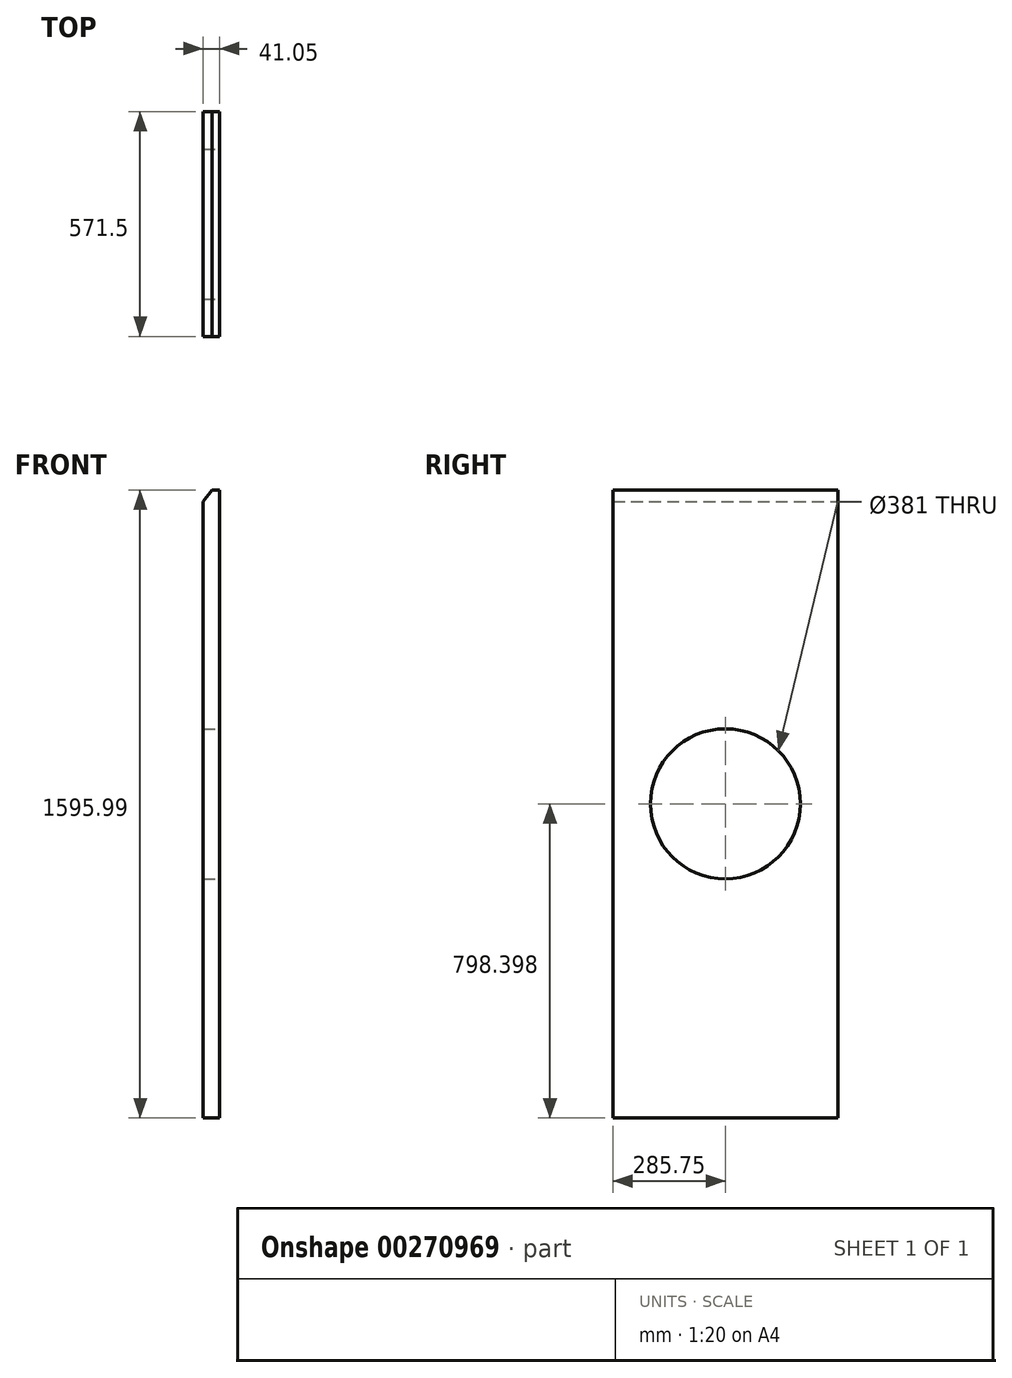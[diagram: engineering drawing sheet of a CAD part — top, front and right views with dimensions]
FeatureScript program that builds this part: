
annotation { "Feature Type Name" : "Feature", "Feature Type Description" : "" }
export const myFeature = defineFeature(function(context is Context, id is Id, definition is map)
    precondition{}
    {
        {
            var Q0;
            Q0=qCreatedBy(makeId("Front.planeOp"),FACE);
            var sketch = newSketch(context, id + "F0", { "sketchPlane" : qUnion([Q0])});
            skLineSegment(sketch, "E0", {"start": v(0, 0) * mm, "end": v(0, 1595.18) * mm});
            skLineSegment(sketch, "E1", {"start": v(0, 1595.18) * mm, "end": v(-19.05, 1595.18) * mm});
            skLineSegment(sketch, "E2", {"start": v(-41.05, 1565.85) * mm, "end": v(-19.05, 1595.18) * mm});
            skLineSegment(sketch, "E3", {"start": v(-41.05, 1565.85) * mm, "end": v(-41.05, -0.8) * mm});
            skLineSegment(sketch, "E4", {"start": v(-41.05, -0.8) * mm, "end": v(0, 0) * mm});
            skSolve(sketch);
        }
        {
            var Q0;
            Q0 = qSketchRegion(id + "F0", true);
            extrude(context, id + "F1", {"entities" : qUnion([Q0]), "depth" : 571.5 * mm});
        }
        {
            var Q0;
            Q0=makeQuery(id+"F1.opExtrude","SWEPT_FACE",FACE,{"disambiguationData":[OSD([sQuery(id+"F0.wireOp",EDGE,"E0")])]});
            var sketch = newSketch(context, id + "F2", { "sketchPlane" : qUnion([Q0])});
            skPoint(sketch, "E5", {"position": v(-285.75, 797.59) * mm});
            skSolve(sketch);
        }
        {
            var Q0;
            Q0=sQuery(id+"F2.wireOp",VERTEX,"E5");
            var Q1;
            Q1=makeQuery(id+"F1.opExtrude","SWEPT_BODY",BODY,{"disambiguationData":[OSD([sQuery(id+"F0.wireOp",EDGE,"E0"),sQuery(id+"F0.wireOp",EDGE,"E1"),sQuery(id+"F0.wireOp",EDGE,"E2"),sQuery(id+"F0.wireOp",EDGE,"E3"),sQuery(id+"F0.wireOp",EDGE,"E4")])]});
            hole(context, id + "F3", {"style" : HoleStyle.SIMPLE, "endStyle" : HoleEndStyle.THROUGH, "holeDiameter" : 381 * mm, "tappedDepth" : 12.7 * mm, "tapClearance" : 3, "locations" : qUnion([Q0]), "scope" : qUnion([Q1])});
        }
    });
